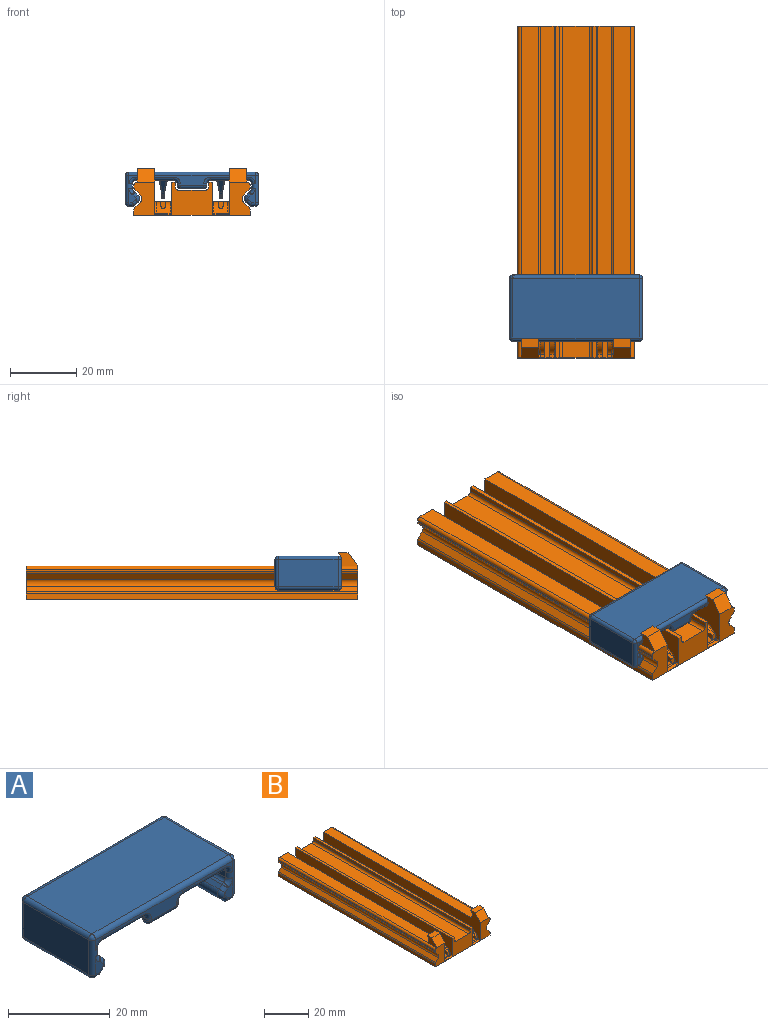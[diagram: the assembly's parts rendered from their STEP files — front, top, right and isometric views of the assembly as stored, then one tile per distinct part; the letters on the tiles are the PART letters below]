
ASSEMBLY  parts=2 mates=1
PART A: 189 faces, bbox 40.2x20.2x10.5 mm
  f0: plane 34.2x18.2mm, normal (0,0,-1), area 506.7mm2, adj f57,f67,f72,f78,f80,f81,f84,f86
  f1: plane 38x2.5mm, normal (0,1,0), area 20.7mm2, adj f47,f48,f65,f66,f72,f77
  f2: plane 4.32x2.17mm, normal (0,1,0), area 4.9mm2, adj f36,f44,f45,f50,f53,f64,f65
  f3: plane 4.32x2.17mm, normal (0,-1,0), area 4.9mm2, adj f51,f52,f62,f63,f70,f75,f76
  f4: plane 4.32x2.17mm, normal (0,-1,0), area 4.9mm2, adj f23,f26,f30,f31,f35,f42,f43
  f5: plane 18x0.8mm, normal (0.71,0,0.71), area 20.3mm2, adj f13,f14,f30,f34
  f6: plane 18x1.47mm, normal (1,0,0), area 26.5mm2, adj f41,f43,f48,f57
  f7: plane 38x18mm, normal (0,0,1), area 684mm2, adj f46,f47,f59,f60
  f8: plane 18x8.29mm, normal (-1,0,0), area 149.3mm2, adj f32,f43,f46,f48
  f9: plane 18x1.09mm, normal (0,0,-1), area 19.5mm2, adj f24,f31,f32,f33
  f10: plane 18x0.94mm, normal (0.71,0,-0.71), area 23.9mm2, adj f14,f23,f24,f25
  f11: plane 38x3mm, normal (0,-1,0), area 39.9mm2, adj f43,f58,f59,f67,f73,f74,f75,f82
  f12: plane 4.32x2.17mm, normal (0,1,0), area 4.9mm2, adj f25,f29,f33,f34,f40,f48,f49
  f13: cylinder r=1.5mm len=18mm, axis (0,1,0), area 8.6mm2, adj f5,f35,f40,f41
  f14: cylinder r=1.5mm len=18mm, axis (0,1,0), area 42.4mm2, adj f5,f10,f26,f29
  f15: plane 18x0.8mm, normal (-0.71,0,0.71), area 20.3mm2, adj f20,f21,f45,f63
  f16: plane 18x1.47mm, normal (-1,0,0), area 26.5mm2, adj f65,f71,f75,f80
  f17: plane 18x8.29mm, normal (1,0,0), area 149.3mm2, adj f60,f61,f65,f75
  f18: plane 18x1.5mm, normal (0,0,-1), area 27mm2, adj f19,f50,f61,f62
  f19: plane 18x1.23mm, normal (-0.71,0,-0.71), area 31.4mm2, adj f18,f21,f44,f51
  f20: cylinder r=1.5mm len=18mm, axis (0,1,0), area 8.6mm2, adj f15,f53,f70,f71
  f21: cylinder r=1.5mm len=18mm, axis (0,1,0), area 42.4mm2, adj f15,f19,f36,f52
  f22: plane 7x0.5mm, normal (0,1,0), area 3.5mm2, adj f73,f81,f82,f87
  f23: cylinder r=1mm len=1.65mm, axis (-0.71,0,-0.71), area 2.1mm2, adj f4,f10,f26,f27
  f24: cylinder r=1mm len=18mm, axis (0,1,0), area 14.1mm2, adj f9,f10,f27,f28
  f25: cylinder r=1mm len=1.65mm, axis (0.71,0,0.71), area 2.1mm2, adj f10,f12,f28,f29
  f26: torus R=0.5mm, axis (0,-1,0), area 2.8mm2, adj f4,f14,f23,f30
  f27: sphere r=1mm, area 0.8mm2, adj f23,f24,f31
  f28: sphere r=1mm, area 1mm2, adj f24,f25,f33
  f29: torus R=0.5mm, axis (0,-1,0), area 2.8mm2, adj f12,f14,f25,f34
  f30: cylinder r=1mm len=1.51mm, axis (0.71,0,-0.71), area 1.8mm2, adj f4,f5,f26,f35
  f31: cylinder r=1mm len=1.09mm, axis (-1,0,0), area 1.7mm2, adj f4,f9,f27,f37
  f32: cylinder r=1mm len=18mm, axis (0,1,0), area 28.3mm2, adj f8,f9,f37,f39
  f33: cylinder r=1mm len=1.09mm, axis (1,0,0), area 1.7mm2, adj f9,f12,f28,f39
  f34: cylinder r=1mm len=1.51mm, axis (-0.71,0,0.71), area 1.8mm2, adj f5,f12,f29,f40
  f35: torus R=0.5mm, axis (0,-1,0), area 0.6mm2, adj f4,f13,f30,f42
  f36: torus R=0.5mm, axis (0,-1,0), area 2.8mm2, adj f2,f21,f44,f45
  f37: sphere r=1mm, area 1.6mm2, adj f31,f32,f43
  f38: sphere r=1mm, area 2.1mm2, adj f46,f47,f48
  f39: sphere r=1mm, area 2.1mm2, adj f32,f33,f48
  f40: torus R=0.5mm, axis (0,-1,0), area 0.6mm2, adj f12,f13,f34,f49
  f41: cylinder r=1mm len=18mm, axis (0,1,0), area 19.9mm2, adj f6,f13,f42,f49
  f42: torus R=2mm, axis (0,-1,0), area 2.4mm2, adj f4,f35,f41,f43
  f43: cylinder r=1mm len=8.29mm, axis (0,0,1), area 15.3mm2, adj f4,f6,f8,f11,f37,f42,f55,f58
  f44: cylinder r=1mm len=1.94mm, axis (-0.71,0,0.71), area 2.4mm2, adj f2,f19,f36,f50
  f45: cylinder r=1mm len=1.51mm, axis (0.71,0,0.71), area 1.8mm2, adj f2,f15,f36,f53
  f46: cylinder r=1mm len=18mm, axis (0,1,0), area 28.3mm2, adj f7,f8,f38,f55
  f47: cylinder r=1mm len=38mm, axis (-1,0,0), area 59.7mm2, adj f1,f7,f38,f56
  f48: cylinder r=1mm len=8.29mm, axis (0,0,-1), area 15.3mm2, adj f1,f6,f8,f12,f38,f39,f49,f66
  f49: torus R=2mm, axis (0,-1,0), area 2.4mm2, adj f12,f40,f41,f48
  f50: cylinder r=1mm len=1.5mm, axis (-1,0,0), area 2mm2, adj f2,f18,f44,f54
  f51: cylinder r=1mm len=1.94mm, axis (0.71,0,-0.71), area 2.4mm2, adj f3,f19,f52,f62
  f52: torus R=0.5mm, axis (0,-1,0), area 2.8mm2, adj f3,f21,f51,f63
  f53: torus R=0.5mm, axis (0,-1,0), area 0.6mm2, adj f2,f20,f45,f64
  f54: sphere r=1mm, area 1mm2, adj f50,f61,f65
  f55: sphere r=1mm, area 1.6mm2, adj f43,f46,f59
  f56: sphere r=1mm, area 1mm2, adj f47,f60,f65
  f57: cylinder r=1mm len=18mm, axis (0,-1,0), area 28.3mm2, adj f0,f6,f58,f66
  f58: torus R=2mm, axis (0,-1,0), area 3.4mm2, adj f11,f43,f57,f67
  f59: cylinder r=1mm len=38mm, axis (1,0,0), area 59.7mm2, adj f7,f11,f55,f68
  f60: cylinder r=1mm len=18mm, axis (0,1,0), area 28.3mm2, adj f7,f17,f56,f68
  f61: cylinder r=1mm len=18mm, axis (0,1,0), area 28.3mm2, adj f17,f18,f54,f69
  f62: cylinder r=1mm len=1.5mm, axis (1,0,0), area 2mm2, adj f3,f18,f51,f69
  f63: cylinder r=1mm len=1.51mm, axis (-0.71,0,-0.71), area 1.8mm2, adj f3,f15,f52,f70
  f64: torus R=2mm, axis (0,-1,0), area 2.4mm2, adj f2,f53,f65,f71
  f65: cylinder r=1mm len=8.29mm, axis (0,0,-1), area 15.3mm2, adj f1,f2,f16,f17,f54,f56,f64,f77
  f66: torus R=2mm, axis (0,-1,0), area 3.4mm2, adj f1,f48,f57,f72
  f67: cylinder r=1mm len=11.5mm, axis (-1,0,0), area 18.1mm2, adj f0,f11,f58,f74
  f68: sphere r=1mm, area 1.6mm2, adj f59,f60,f75
  f69: sphere r=1mm, area 1.6mm2, adj f61,f62,f75
  f70: torus R=0.5mm, axis (0,-1,0), area 0.6mm2, adj f3,f20,f63,f76
  f71: cylinder r=1mm len=18mm, axis (0,1,0), area 19.9mm2, adj f16,f20,f64,f76
  f72: cylinder r=1mm len=34mm, axis (1,0,0), area 53.4mm2, adj f0,f1,f66,f77
  f73: cylinder r=1mm len=2mm, axis (0,0,1), area 1.6mm2, adj f11,f22,f74,f78,f79
  f74: torus R=2mm, axis (0,-1,0), area 3.4mm2, adj f11,f67,f73,f78
  f75: cylinder r=1mm len=8.29mm, axis (0,0,1), area 15.3mm2, adj f3,f11,f16,f17,f68,f69,f76,f83
  f76: torus R=2mm, axis (0,-1,0), area 2.4mm2, adj f3,f70,f71,f75
  f77: torus R=2mm, axis (0,-1,0), area 3.4mm2, adj f1,f65,f72,f80
  f78: torus R=2mm, axis (0,0,1), area 3.4mm2, adj f0,f73,f74,f81
  f79: sphere r=1mm, area 3.1mm2, adj f73,f82
  f80: cylinder r=1mm len=18mm, axis (0,-1,0), area 28.3mm2, adj f0,f16,f77,f83
  f81: cylinder r=1mm len=7mm, axis (-1,0,0), area 11mm2, adj f0,f22,f78,f84
  f82: cylinder r=1mm len=7mm, axis (-1,0,0), area 22mm2, adj f11,f22,f79,f85
  f83: torus R=2mm, axis (0,-1,0), area 3.4mm2, adj f11,f75,f80,f86
  f84: torus R=2mm, axis (0,0,1), area 3.4mm2, adj f0,f81,f87,f88
  f85: sphere r=1mm, area 1.6mm2, adj f82,f87
  f86: cylinder r=1mm len=11.5mm, axis (-1,0,0), area 18.1mm2, adj f0,f11,f83,f88
  f87: cylinder r=1mm len=2mm, axis (0,0,-1), area 1.6mm2, adj f11,f22,f84,f85,f88
  f88: torus R=2mm, axis (0,-1,0), area 3.4mm2, adj f11,f84,f86,f87
  f89: plane 3.46x0.4mm, normal (0,0,-1), area 1.4mm2, adj f90,f96,f118,f150
  f90: cylinder r=0.1mm len=0.4mm, axis (1,0,0), area 0.1mm2, adj f89,f91,f114,f149
  f91: plane 0.4x0.14mm, normal (0,1,0), area 0.1mm2, adj f90,f92,f113,f145
  f92: cylinder r=0.3mm len=0.4mm, axis (1,0,0), area 0.2mm2, adj f91,f93,f117,f144
  f93: extruded ~1.26x0.97mm, area 0.7mm2, adj f92,f94,f119,f143
  f94: plane 3.7x1.76mm, normal (0,1,0), area 3.6mm2, adj f93,f121,f124,f126,f131,f136,f139,f141
  f95: plane 10.09x5.05mm, normal (0,-0.45,-0.89), area 11.1mm2, adj f96,f122,f125,f127,f132,f137,f140,f142
  f96: cylinder r=4mm len=1.79mm, axis (1,0,0), area 0.7mm2, adj f89,f95,f120,f146
  f97: plane 7.23x1.67mm, normal (-1,0,0), area 7.6mm2, adj f118,f119,f120,f121,f122,f123
  f98: plane 12.68x3.23mm, normal (-0.98,0,-0.21), area 31.2mm2, adj f123,f126,f127,f128
  f99: plane 12.68x3.23mm, normal (0.98,0,-0.21), area 31.2mm2, adj f133,f136,f137,f138
  f100: plane 7.23x1.67mm, normal (1,0,0), area 7.6mm2, adj f138,f141,f142,f143,f146,f150
  f101: plane 3.46x0.4mm, normal (0,0,-1), area 1.4mm2, adj f102,f108,f156,f188
  f102: cylinder r=0.1mm len=0.4mm, axis (-1,0,0), area 0.1mm2, adj f101,f103,f152,f187
  f103: plane 0.4x0.14mm, normal (0,1,0), area 0.1mm2, adj f102,f104,f151,f183
  f104: cylinder r=0.3mm len=0.4mm, axis (-1,0,0), area 0.2mm2, adj f103,f105,f155,f182
  f105: extruded ~1.26x0.97mm, area 0.7mm2, adj f104,f106,f157,f181
  f106: plane 3.7x1.76mm, normal (0,1,0), area 3.6mm2, adj f105,f159,f162,f164,f169,f174,f177,f179
  f107: plane 10.09x5.05mm, normal (0,-0.45,-0.89), area 11.1mm2, adj f108,f160,f163,f165,f170,f175,f178,f180
  f108: cylinder r=4mm len=1.79mm, axis (-1,0,0), area 0.7mm2, adj f101,f107,f158,f184
  f109: plane 7.23x1.67mm, normal (1,0,0), area 7.6mm2, adj f176,f179,f180,f181,f184,f188
  f110: plane 12.68x3.23mm, normal (0.98,0,-0.21), area 31.2mm2, adj f171,f174,f175,f176
  f111: plane 12.68x3.23mm, normal (-0.98,0,-0.21), area 31.2mm2, adj f161,f164,f165,f166
  f112: plane 7.23x1.67mm, normal (-1,0,0), area 7.6mm2, adj f156,f157,f158,f159,f160,f161
  f113: cylinder r=0.3mm len=0.28mm, axis (0,0,-1), area 0mm2, adj f91,f114,f117
  f114: bspline ~0.35x0.25mm, area 0mm2, adj f90,f113,f115,f118
  f115: bspline ~0.12x0.09mm, area 0mm2, adj f114,f116,f117,f118
  f116: bspline ~0.51x0.09mm, area 0mm2, adj f115,f118,f119
  f117: sphere r=0.3mm, area 0.1mm2, adj f92,f113,f115,f119
  f118: cylinder r=0.3mm len=3.46mm, axis (0,1,0), area 1.6mm2, adj f89,f97,f114,f115,f116,f120
  f119: bspline ~1.64x1.56mm, area 0.9mm2, adj f93,f97,f116,f117,f121
  f120: torus R=3.7mm, axis (1,0,0), area 0.9mm2, adj f96,f97,f118,f122
  f121: cylinder r=0.3mm len=0.47mm, axis (0,0,1), area 0.2mm2, adj f94,f97,f119,f124
  f122: cylinder r=0.3mm len=2.69mm, axis (0,0.89,-0.45), area 1.3mm2, adj f95,f97,f120,f125
  f123: cylinder r=0.3mm len=6.22mm, axis (0,1,0), area 0.4mm2, adj f97,f98,f124,f125
  f124: torus R=0.6mm, axis (0,-1,0), area 0mm2, adj f94,f121,f123,f126
  f125: bspline ~0.39x0.33mm, area 0.1mm2, adj f95,f122,f123,f127
  f126: cylinder r=0.3mm len=3.29mm, axis (-0.21,0,0.98), area 1.5mm2, adj f94,f98,f124,f129
  f127: cylinder r=0.3mm len=7.42mm, axis (0.1,0.89,-0.45), area 3.3mm2, adj f95,f98,f125,f130
  f128: cylinder r=0.3mm len=12.68mm, axis (0,1,0), area 5.2mm2, adj f0,f98,f129,f130
  f129: bspline ~0.64x0.6mm, area 0.3mm2, adj f0,f126,f128,f131
  f130: bspline ~1.09x0.5mm, area 0.3mm2, adj f0,f127,f128,f132
  f131: cylinder r=0.3mm len=1.76mm, axis (-1,0,0), area 0.8mm2, adj f0,f94,f129,f134
  f132: cylinder r=0.3mm len=1.99mm, axis (-1,0,0), area 0.3mm2, adj f0,f95,f130,f135
  f133: cylinder r=0.3mm len=12.68mm, axis (0,-1,0), area 5.2mm2, adj f0,f99,f134,f135
  f134: bspline ~0.72x0.7mm, area 0.3mm2, adj f0,f131,f133,f136
  f135: bspline ~1.09x0.5mm, area 0.3mm2, adj f0,f132,f133,f137
  f136: cylinder r=0.3mm len=3.29mm, axis (-0.21,0,-0.98), area 1.5mm2, adj f94,f99,f134,f139
  f137: cylinder r=0.3mm len=7.42mm, axis (0.1,-0.89,0.45), area 3.3mm2, adj f95,f99,f135,f140
  f138: cylinder r=0.3mm len=6.22mm, axis (0,1,0), area 0.4mm2, adj f99,f100,f139,f140
  f139: torus R=0.6mm, axis (0,-1,0), area 0mm2, adj f94,f136,f138,f141
  f140: bspline ~0.39x0.33mm, area 0.1mm2, adj f95,f137,f138,f142
  f141: cylinder r=0.3mm len=0.47mm, axis (0,0,-1), area 0.2mm2, adj f94,f100,f139,f143
  f142: cylinder r=0.3mm len=2.69mm, axis (0,-0.89,0.45), area 1.3mm2, adj f95,f100,f140,f146
  f143: bspline ~1.84x1.39mm, area 0.9mm2, adj f93,f100,f141,f144,f147
  f144: sphere r=0.3mm, area 0.1mm2, adj f92,f143,f145,f148
  f145: cylinder r=0.3mm len=0.28mm, axis (0,0,-1), area 0mm2, adj f91,f144,f149
  f146: torus R=3.7mm, axis (1,0,0), area 0.9mm2, adj f96,f100,f142,f150
  f147: bspline ~0.51x0.09mm, area 0mm2, adj f143,f148,f150
  f148: bspline ~0.12x0.09mm, area 0mm2, adj f144,f147,f149,f150
  f149: bspline ~0.35x0.25mm, area 0mm2, adj f90,f145,f148,f150
  f150: cylinder r=0.3mm len=3.46mm, axis (0,-1,0), area 1.6mm2, adj f89,f100,f146,f147,f148,f149
  f151: cylinder r=0.3mm len=0.28mm, axis (0,0,1), area 0mm2, adj f103,f152,f155
  f152: bspline ~0.31x0.25mm, area 0mm2, adj f102,f151,f153,f156
  f153: bspline ~0.12x0.09mm, area 0mm2, adj f152,f154,f155,f156
  f154: bspline ~0.51x0.09mm, area 0mm2, adj f153,f156,f157
  f155: sphere r=0.3mm, area 0.1mm2, adj f104,f151,f153,f157
  f156: cylinder r=0.3mm len=3.46mm, axis (0,-1,0), area 1.6mm2, adj f101,f112,f152,f153,f154,f158
  f157: bspline ~1.84x1.61mm, area 0.9mm2, adj f105,f112,f154,f155,f159
  f158: torus R=3.7mm, axis (-1,0,0), area 0.9mm2, adj f108,f112,f156,f160
  f159: cylinder r=0.3mm len=0.47mm, axis (0,0,-1), area 0.2mm2, adj f106,f112,f157,f162
  f160: cylinder r=0.3mm len=2.69mm, axis (0,-0.89,0.45), area 1.3mm2, adj f107,f112,f158,f163
  f161: cylinder r=0.3mm len=6.22mm, axis (0,1,0), area 0.4mm2, adj f111,f112,f162,f163
  f162: torus R=0.6mm, axis (0,-1,0), area 0mm2, adj f106,f159,f161,f164
  f163: bspline ~0.39x0.33mm, area 0.1mm2, adj f107,f160,f161,f165
  f164: cylinder r=0.3mm len=3.29mm, axis (0.21,0,-0.98), area 1.5mm2, adj f106,f111,f162,f167
  f165: cylinder r=0.3mm len=7.42mm, axis (-0.1,-0.89,0.45), area 3.3mm2, adj f107,f111,f163,f168
  f166: cylinder r=0.3mm len=12.68mm, axis (0,-1,0), area 5.2mm2, adj f0,f111,f167,f168
  f167: bspline ~0.72x0.63mm, area 0.3mm2, adj f0,f164,f166,f169
  f168: bspline ~1.09x0.5mm, area 0.3mm2, adj f0,f165,f166,f170
  f169: cylinder r=0.3mm len=1.76mm, axis (1,0,0), area 0.8mm2, adj f0,f106,f167,f172
  f170: cylinder r=0.3mm len=1.99mm, axis (1,0,0), area 0.3mm2, adj f0,f107,f168,f173
  f171: cylinder r=0.3mm len=12.68mm, axis (0,1,0), area 5.2mm2, adj f0,f110,f172,f173
  f172: bspline ~0.64x0.6mm, area 0.3mm2, adj f0,f169,f171,f174
  f173: bspline ~1.09x0.5mm, area 0.3mm2, adj f0,f170,f171,f175
  f174: cylinder r=0.3mm len=3.29mm, axis (0.21,0,0.98), area 1.5mm2, adj f106,f110,f172,f177
  f175: cylinder r=0.3mm len=7.42mm, axis (-0.1,0.89,-0.45), area 3.3mm2, adj f107,f110,f173,f178
  f176: cylinder r=0.3mm len=6.22mm, axis (0,1,0), area 0.4mm2, adj f109,f110,f177,f178
  f177: torus R=0.6mm, axis (0,-1,0), area 0mm2, adj f106,f174,f176,f179
  f178: bspline ~0.39x0.33mm, area 0.1mm2, adj f107,f175,f176,f180
  f179: cylinder r=0.3mm len=0.47mm, axis (0,0,1), area 0.2mm2, adj f106,f109,f177,f181
  f180: cylinder r=0.3mm len=2.69mm, axis (0,0.89,-0.45), area 1.3mm2, adj f107,f109,f178,f184
  f181: bspline ~1.84x1.39mm, area 0.9mm2, adj f105,f109,f179,f182,f185
  f182: sphere r=0.3mm, area 0.1mm2, adj f104,f181,f183,f186
  f183: cylinder r=0.3mm len=0.28mm, axis (0,0,1), area 0mm2, adj f103,f182,f187
  f184: torus R=3.7mm, axis (-1,0,0), area 0.9mm2, adj f108,f109,f180,f188
  f185: bspline ~0.51x0.09mm, area 0mm2, adj f181,f186,f188
  f186: bspline ~0.12x0.09mm, area 0mm2, adj f182,f185,f187,f188
  f187: bspline ~0.31x0.25mm, area 0mm2, adj f102,f183,f186,f188
  f188: cylinder r=0.3mm len=3.46mm, axis (0,1,0), area 1.6mm2, adj f101,f109,f184,f185,f186,f187
PART B: 72 faces, bbox 35x100x14 mm
  f0: plane 94x5.3mm, normal (0,0,1), area 498.2mm2, adj f6,f29,f33,f71
  f1: plane 94x5.3mm, normal (0,0,1), area 498.2mm2, adj f6,f30,f31,f67
  f2: plane 35x10mm, normal (0,-1,0), area 209.5mm2, adj f5,f8,f9,f10,f11,f12,f13,f14
  f3: plane 2x1.3mm, normal (0,-1,0), area 2.4mm2, adj f4,f36,f37,f38
  f4: plane 100x4.2mm, normal (0,0,1), area 401.5mm2, adj f3,f6,f36,f38,f44,f55,f61
  f5: plane 100x1.2mm, normal (0,0,1), area 120mm2, adj f2,f6,f22,f35
  f6: plane 35x10mm, normal (0,1,0), area 248mm2, adj f0,f1,f4,f5,f8,f9,f10,f11
  f7: plane 2x1.3mm, normal (0,-1,0), area 2.4mm2, adj f34,f41,f42,f43
  f8: plane 100x1.2mm, normal (0,0,1), area 120mm2, adj f2,f6,f20,f32
  f9: plane 100x0.59mm, normal (1,0,0), area 58.6mm2, adj f2,f6,f27,f30
  f10: plane 100x0.59mm, normal (-1,0,0), area 58.6mm2, adj f2,f6,f25,f29
  f11: plane 100x1.59mm, normal (1,0,0), area 158.6mm2, adj f2,f6,f13,f28
  f12: plane 100x1.59mm, normal (-1,0,0), area 158.6mm2, adj f2,f6,f13,f26
  f13: plane 100x35mm, normal (0,0,-1), area 3500mm2, adj f2,f6,f11,f12
  f14: plane 100x1.65mm, normal (-0.71,0,-0.71), area 232.8mm2, adj f2,f6,f18,f25
  f15: plane 100x1.65mm, normal (-0.71,0,0.71), area 232.8mm2, adj f2,f6,f18,f26
  f16: plane 100x1.65mm, normal (0.71,0,-0.71), area 232.8mm2, adj f2,f6,f19,f27
  f17: plane 100x1.65mm, normal (0.71,0,0.71), area 232.8mm2, adj f2,f6,f19,f28
  f18: cylinder r=1.5mm len=100mm, axis (0,-1,0), area 235.6mm2, adj f2,f6,f14,f15
  f19: cylinder r=1.5mm len=100mm, axis (0,-1,0), area 235.6mm2, adj f2,f6,f16,f17
  f20: plane 100x1.5mm, normal (-1,0,0), area 150mm2, adj f2,f6,f8,f23
  f21: plane 100x8mm, normal (0,0,1), area 800mm2, adj f2,f6,f23,f24
  f22: plane 100x1.5mm, normal (1,0,0), area 150mm2, adj f2,f5,f6,f24
  f23: cylinder r=1mm len=100mm, axis (0,1,0), area 157.1mm2, adj f2,f6,f20,f21
  f24: cylinder r=1mm len=100mm, axis (0,-1,0), area 157.1mm2, adj f2,f6,f21,f22
  f25: cylinder r=1mm len=100mm, axis (0,1,0), area 78.5mm2, adj f2,f6,f10,f14
  f26: cylinder r=1mm len=100mm, axis (0,1,0), area 78.5mm2, adj f2,f6,f12,f15
  f27: cylinder r=1mm len=100mm, axis (0,1,0), area 78.5mm2, adj f2,f6,f9,f16
  f28: cylinder r=1mm len=100mm, axis (0,1,0), area 78.5mm2, adj f2,f6,f11,f17
  f29: cylinder r=1mm len=100mm, axis (0,1,0), area 157.1mm2, adj f0,f2,f6,f10,f68
  f30: cylinder r=1mm len=100mm, axis (0,-1,0), area 157.1mm2, adj f1,f2,f6,f9,f64
  f31: plane 100x13.45mm, normal (-1,0,0), area 585.1mm2, adj f1,f2,f6,f59,f61,f63,f65,f66
  f32: plane 100x9.45mm, normal (1,0,0), area 569.9mm2, adj f2,f6,f8,f55,f56,f57
  f33: plane 100x13.45mm, normal (1,0,0), area 585.1mm2, adj f0,f2,f6,f51,f53,f54,f69,f70
  f34: plane 100x4.2mm, normal (0,0,1), area 401.5mm2, adj f6,f7,f41,f43,f45,f46,f54
  f35: plane 100x9.45mm, normal (-1,0,0), area 569.9mm2, adj f2,f5,f6,f46,f47,f48
  f36: plane 6.37x1.35mm, normal (1,0,0), area 5.4mm2, adj f3,f4,f37,f44
  f37: cylinder r=0.65mm len=2.95mm, axis (0,-1,0), area 5.2mm2, adj f3,f36,f38,f44
  f38: plane 6.37x1.35mm, normal (-1,0,0), area 5.4mm2, adj f3,f4,f37,f44
  f39: plane 4.2x1.19mm, normal (0,0,1), area 5mm2, adj f2,f56,f59,f60
  f40: plane 4.2x1.19mm, normal (0,0,1), area 5mm2, adj f2,f48,f50,f51
  f41: plane 6.37x1.35mm, normal (1,0,0), area 5.4mm2, adj f7,f34,f42,f45
  f42: cylinder r=0.65mm len=2.95mm, axis (0,-1,0), area 5.2mm2, adj f7,f41,f43,f45
  f43: plane 6.37x1.35mm, normal (-1,0,0), area 5.4mm2, adj f7,f34,f42,f45
  f44: cylinder r=5mm len=4.79mm, axis (-1,0,0), area 21.1mm2, adj f4,f36,f37,f38,f57,f60,f63
  f45: cylinder r=5mm len=4.79mm, axis (1,0,0), area 21.1mm2, adj f34,f41,f42,f43,f47,f50,f53
  f46: cylinder r=0.4mm len=93.63mm, axis (0,1,0), area 58.8mm2, adj f6,f34,f35,f47
  f47: torus R=5.4mm, axis (1,0,0), area 4.1mm2, adj f35,f45,f46,f49
  f48: cylinder r=0.4mm len=1.19mm, axis (0,1,0), area 0.7mm2, adj f2,f35,f40,f49
  f49: sphere r=0.4mm, area 0.2mm2, adj f47,f48,f50
  f50: cylinder r=0.4mm len=4.2mm, axis (1,0,0), area 2.1mm2, adj f40,f45,f49,f52
  f51: cylinder r=0.4mm len=1.19mm, axis (0,-1,0), area 0.7mm2, adj f2,f33,f40,f52
  f52: sphere r=0.4mm, area 0.2mm2, adj f50,f51,f53
  f53: torus R=5.4mm, axis (1,0,0), area 4.1mm2, adj f33,f45,f52,f54
  f54: cylinder r=0.4mm len=93.63mm, axis (0,-1,0), area 58.8mm2, adj f6,f33,f34,f53
  f55: cylinder r=0.4mm len=93.63mm, axis (0,1,0), area 58.8mm2, adj f4,f6,f32,f57
  f56: cylinder r=0.4mm len=1.19mm, axis (0,1,0), area 0.7mm2, adj f2,f32,f39,f58
  f57: torus R=5.4mm, axis (1,0,0), area 4.1mm2, adj f32,f44,f55,f58
  f58: sphere r=0.4mm, area 0.2mm2, adj f56,f57,f60
  f59: cylinder r=0.4mm len=1.19mm, axis (0,-1,0), area 0.7mm2, adj f2,f31,f39,f62
  f60: cylinder r=0.4mm len=4.2mm, axis (-1,0,0), area 2.1mm2, adj f39,f44,f58,f62
  f61: cylinder r=0.4mm len=93.63mm, axis (0,-1,0), area 58.8mm2, adj f4,f6,f31,f63
  f62: sphere r=0.4mm, area 0.2mm2, adj f59,f60,f63
  f63: torus R=5.4mm, axis (1,0,0), area 4.1mm2, adj f31,f44,f61,f62
  f64: plane 6x4mm, normal (1,0,0), area 15.2mm2, adj f30,f65,f66,f67
  f65: plane 5.3x3mm, normal (0,0,1), area 15.9mm2, adj f31,f64,f66,f67
  f66: plane 5.3x4mm, normal (0,-0.8,0.6), area 26.5mm2, adj f2,f31,f64,f65
  f67: cylinder r=2.5mm len=5.3mm, axis (-1,0,0), area 24.6mm2, adj f1,f31,f64,f65
  f68: plane 6x4mm, normal (-1,0,0), area 15.2mm2, adj f29,f69,f70,f71
  f69: plane 5.3x3mm, normal (0,0,1), area 15.9mm2, adj f33,f68,f70,f71
  f70: plane 5.3x4mm, normal (0,-0.8,0.6), area 26.5mm2, adj f2,f33,f68,f69
  f71: cylinder r=2.5mm len=5.3mm, axis (-1,0,0), area 24.6mm2, adj f0,f33,f68,f69
PLACE A t=(-18.37,-53.88,0.31)mm
PLACE B t=(-18.37,-18.88,0.31)mm
MATE slider A.f11 <-> B.f2  axis (0,-1,0) through (-18.37,-63.88,10.31)mm
